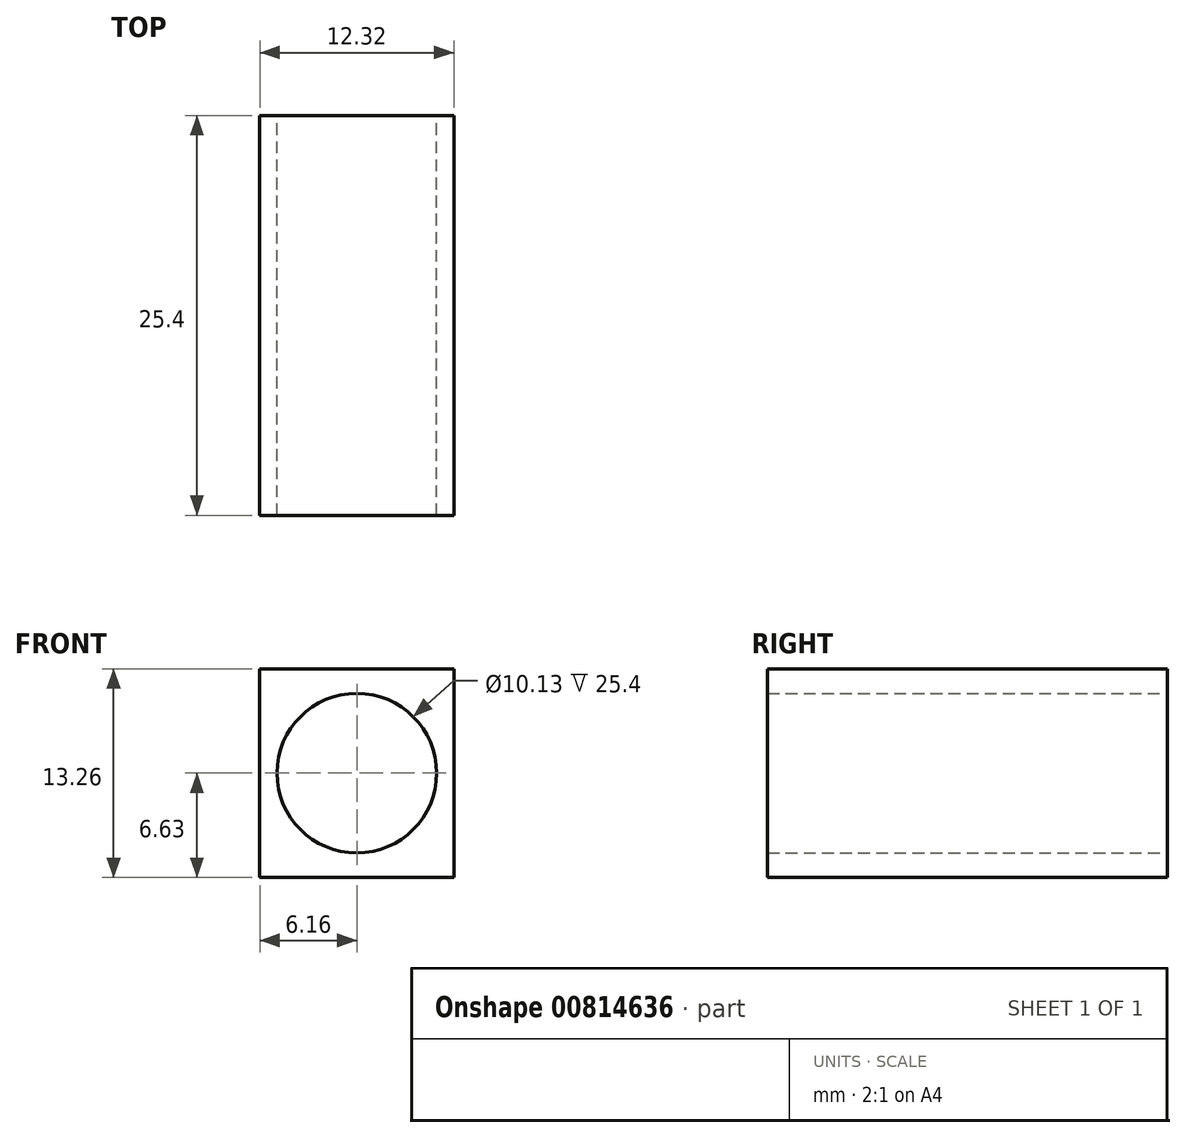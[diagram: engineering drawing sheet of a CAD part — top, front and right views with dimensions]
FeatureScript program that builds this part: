
annotation { "Feature Type Name" : "Feature", "Feature Type Description" : "" }
export const myFeature = defineFeature(function(context is Context, id is Id, definition is map)
    precondition{}
    {
        {
            var Q0;
            Q0=qCreatedBy(makeId("Front.planeOp"),FACE);
            var sketch = newSketch(context, id + "F0", { "sketchPlane" : qUnion([Q0])});
            skCircle(sketch, "E0", {"center": v(0, 0) * mm, "radius": 5.07 * mm});
            skLineSegment(sketch, "E1.bottom", {"start": v(6.16, -6.63) * mm, "end": v(-6.16, -6.63) * mm});
            skLineSegment(sketch, "E1.top", {"start": v(6.16, 6.63) * mm, "end": v(-6.16, 6.63) * mm});
            skLineSegment(sketch, "E1.left", {"start": v(6.16, -6.63) * mm, "end": v(6.16, 6.63) * mm});
            skLineSegment(sketch, "E1.right", {"start": v(-6.16, -6.63) * mm, "end": v(-6.16, 6.63) * mm});
            skSolve(sketch);
        }
        {
            var Q0;
            Q0 = qSketchRegion(id + "F0", true);
            extrude(context, id + "F1", {"entities" : qUnion([Q0]), "depth" : 25.4 * mm, "offsetDistance" : 25.4 * mm});
        }
    });
